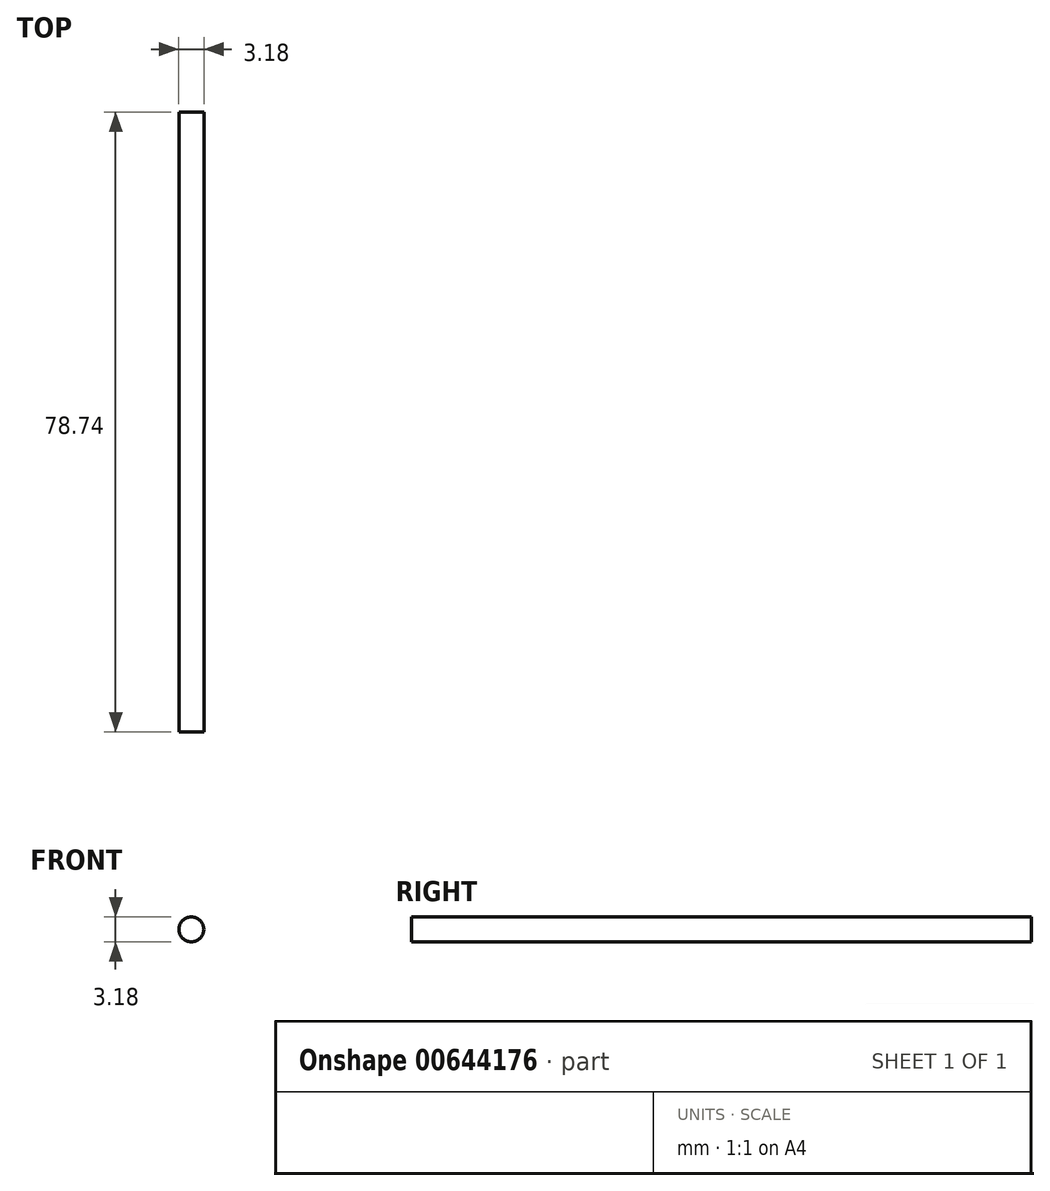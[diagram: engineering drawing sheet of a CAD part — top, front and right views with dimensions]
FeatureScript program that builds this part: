
annotation { "Feature Type Name" : "Feature", "Feature Type Description" : "" }
export const myFeature = defineFeature(function(context is Context, id is Id, definition is map)
    precondition{}
    {
        {
            var Q0;
            Q0=qCreatedBy(makeId("Front.planeOp"),FACE);
            var sketch = newSketch(context, id + "F0", { "sketchPlane" : qUnion([Q0])});
            skPoint(sketch, "E0", {"position": v(0, 0) * mm});
            skCircle(sketch, "E1", {"center": v(0, 0) * mm, "radius": 1.59 * mm});
            skSolve(sketch);
        }
        {
            var Q0;
            Q0 = qSketchRegion(id + "F0", true);
            extrude(context, id + "F1", {"entities" : qUnion([Q0]), "depth" : 78.74 * mm, "offsetDistance" : 25.4 * mm});
        }
    });
